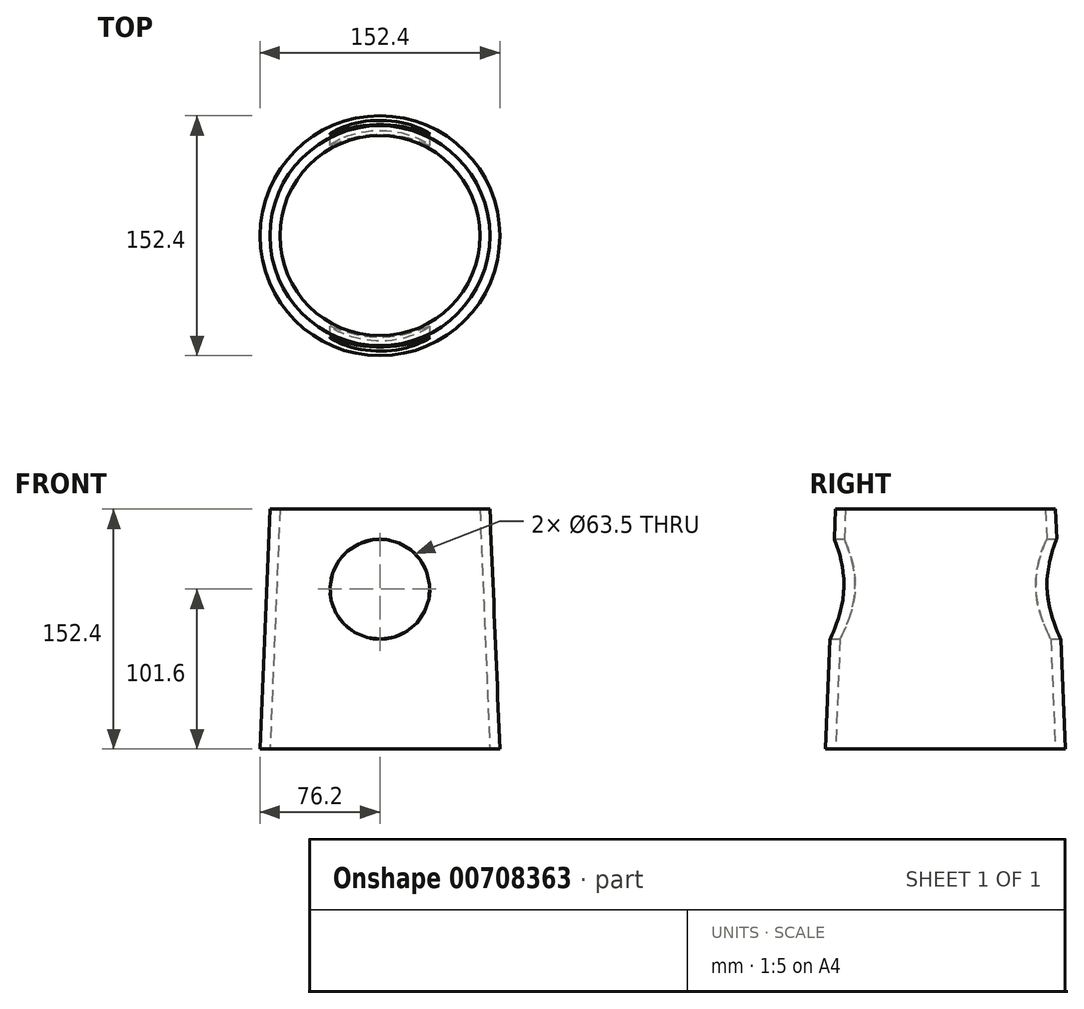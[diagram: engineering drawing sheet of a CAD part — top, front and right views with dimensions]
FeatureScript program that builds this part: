
annotation { "Feature Type Name" : "Feature", "Feature Type Description" : "" }
export const myFeature = defineFeature(function(context is Context, id is Id, definition is map)
    precondition{}
    {
        {
            var Q0;
            Q0=qCreatedBy(makeId("Top.planeOp"),FACE);
            cPlane(context, id + "F0", {"entities" : qUnion([Q0]), "cplaneType" : CPlaneType.OFFSET, "offset" : 152.4 * mm, "width" : 152.4 * mm, "height" : 152.4 * mm});
        }
        {
            var Q0;
            Q0=qCreatedBy(id+"F0.planeOp",FACE);
            var sketch = newSketch(context, id + "F1", { "sketchPlane" : qUnion([Q0])});
            skCircle(sketch, "E0", {"center": v(0, 0) * mm, "radius": 63.5 * mm});
            skSolve(sketch);
        }
        {
            var Q0;
            Q0=qCreatedBy(makeId("Top.planeOp"),FACE);
            var sketch = newSketch(context, id + "F2", { "sketchPlane" : qUnion([Q0])});
            skCircle(sketch, "E1", {"center": v(0, 0) * mm, "radius": 69.85 * mm});
            skSolve(sketch);
        }
        {
            var Q0;
            Q0=qCreatedBy(id+"F0.planeOp",FACE);
            var sketch = newSketch(context, id + "F3", { "sketchPlane" : qUnion([Q0])});
            skCircle(sketch, "E2", {"center": v(0, 0) * mm, "radius": 69.85 * mm});
            skSolve(sketch);
        }
        {
            var Q0;
            Q0=makeQuery(id+"F2.imprint","IMPRINT",FACE,{"disambiguationData":[TD([[makeQuery(id+"F2.imprint","IMPRINT",EDGE,{"derivedFrom":sQuery(id+"F2.wireOp",EDGE,"E1")}),1.0]])]});
            var sketch = newSketch(context, id + "F4", { "sketchPlane" : qUnion([Q0])});
            skCircle(sketch, "E3", {"center": v(0, 0) * mm, "radius": 76.2 * mm});
            skSolve(sketch);
        }
        {
            var Q0;
            Q0=makeQuery(id+"F3.imprint","IMPRINT",FACE,{"disambiguationData":[TD([[makeQuery(id+"F3.imprint","IMPRINT",EDGE,{"derivedFrom":sQuery(id+"F3.wireOp",EDGE,"E2")}),1.0]])]});
            var Q1;
            Q1 = qSketchRegion(id + "F4", true);
            loft(context, id + "F5", {"sheetProfilesArray" : [{ "sheetProfileEntities" : qUnion([Q0]) }, { "sheetProfileEntities" : qUnion([Q1]) }]});
        }
        {
            var Q1;
            Q1=makeQuery(id+"F1.imprint","IMPRINT",FACE,{"disambiguationData":[TD([[makeQuery(id+"F1.imprint","IMPRINT",EDGE,{"derivedFrom":sQuery(id+"F1.wireOp",EDGE,"E0")}),1.0]])]});
            var Q2;
            Q2 = qSketchRegion(id + "F2", true);
            loft(context, id + "F6", {"operationType" : NewBodyOperationType.REMOVE, "sheetProfilesArray" : [{ "sheetProfileEntities" : qUnion([Q1]) }, { "sheetProfileEntities" : qUnion([Q2]) }]});
        }
        {
            var Q0;
            Q0=qCreatedBy(makeId("Front.planeOp"),FACE);
            var sketch = newSketch(context, id + "F7", { "sketchPlane" : qUnion([Q0])});
            skCircle(sketch, "E4", {"center": v(0, 101.6) * mm, "radius": 31.75 * mm});
            skSolve(sketch);
        }
        {
            var Q0;
            Q0 = qSketchRegion(id + "F7", true);
            extrude(context, id + "F8", {"entities" : qUnion([Q0]), "operationType" : NewBodyOperationType.REMOVE, "depth" : 127 * mm, "offsetDistance" : 25.4 * mm, "hasSecondDirection" : true, "secondDirectionOppositeDirection" : true, "secondDirectionDepth" : 127 * mm});
        }
    });
